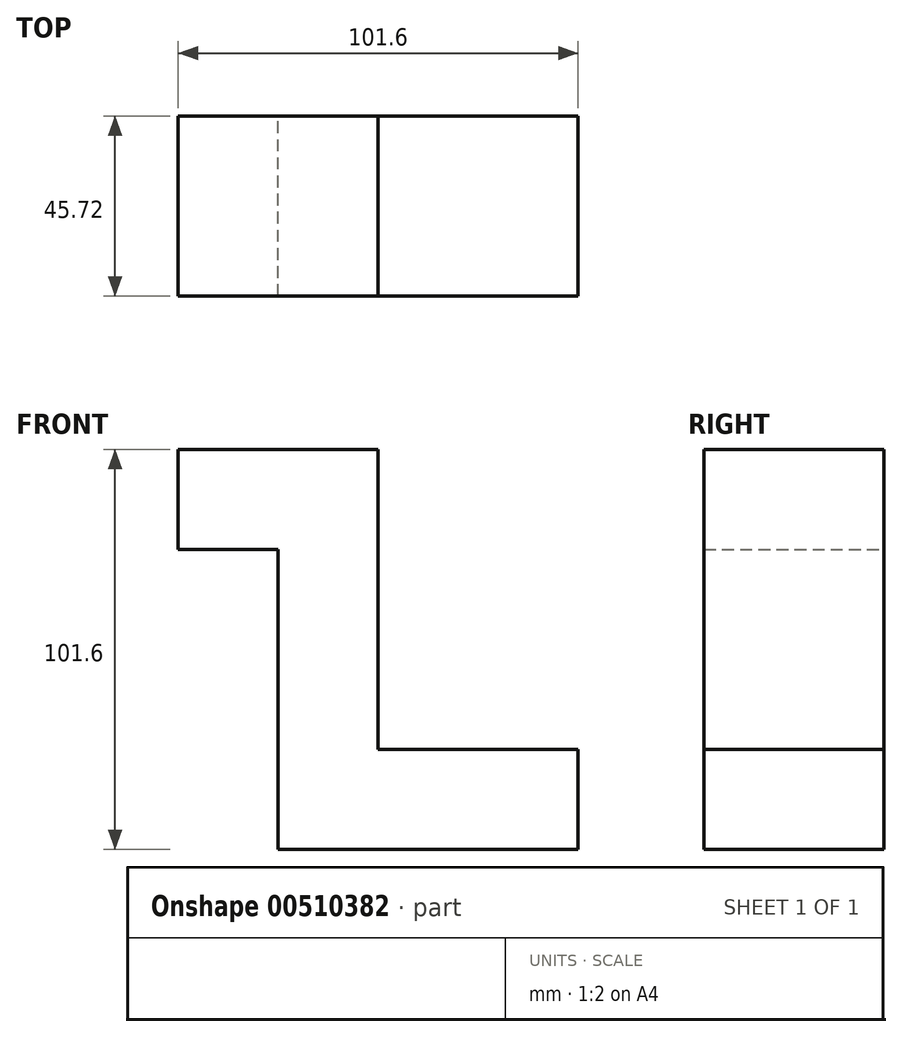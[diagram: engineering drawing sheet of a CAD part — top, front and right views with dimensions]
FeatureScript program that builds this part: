
annotation { "Feature Type Name" : "Feature", "Feature Type Description" : "" }
export const myFeature = defineFeature(function(context is Context, id is Id, definition is map)
    precondition{}
    {
        {
            var Q0;
            Q0=qCreatedBy(makeId("Front.planeOp"),FACE);
            var sketch = newSketch(context, id + "F0", { "sketchPlane" : qUnion([Q0])});
            skLineSegment(sketch, "E0", {"start": v(-50.8, 53.8) * mm, "end": v(0, 53.8) * mm});
            skLineSegment(sketch, "E1", {"start": v(0, 53.8) * mm, "end": v(0, -22.4) * mm});
            skLineSegment(sketch, "E2", {"start": v(0, -22.4) * mm, "end": v(50.8, -22.4) * mm});
            skLineSegment(sketch, "E3", {"start": v(50.8, -22.4) * mm, "end": v(50.8, -47.8) * mm});
            skLineSegment(sketch, "E4", {"start": v(50.8, -47.8) * mm, "end": v(-25.4, -47.8) * mm});
            skLineSegment(sketch, "E5", {"start": v(-25.4, -47.8) * mm, "end": v(-25.4, 28.4) * mm});
            skLineSegment(sketch, "E6", {"start": v(-25.4, 28.4) * mm, "end": v(-50.8, 28.4) * mm});
            skLineSegment(sketch, "E7", {"start": v(-50.8, 28.4) * mm, "end": v(-50.8, 53.8) * mm});
            skSolve(sketch);
        }
        {
            var Q0;
            Q0 = qSketchRegion(id + "F0", true);
            extrude(context, id + "F1", {"entities" : qUnion([Q0]), "depth" : 45.72 * mm});
        }
    });
